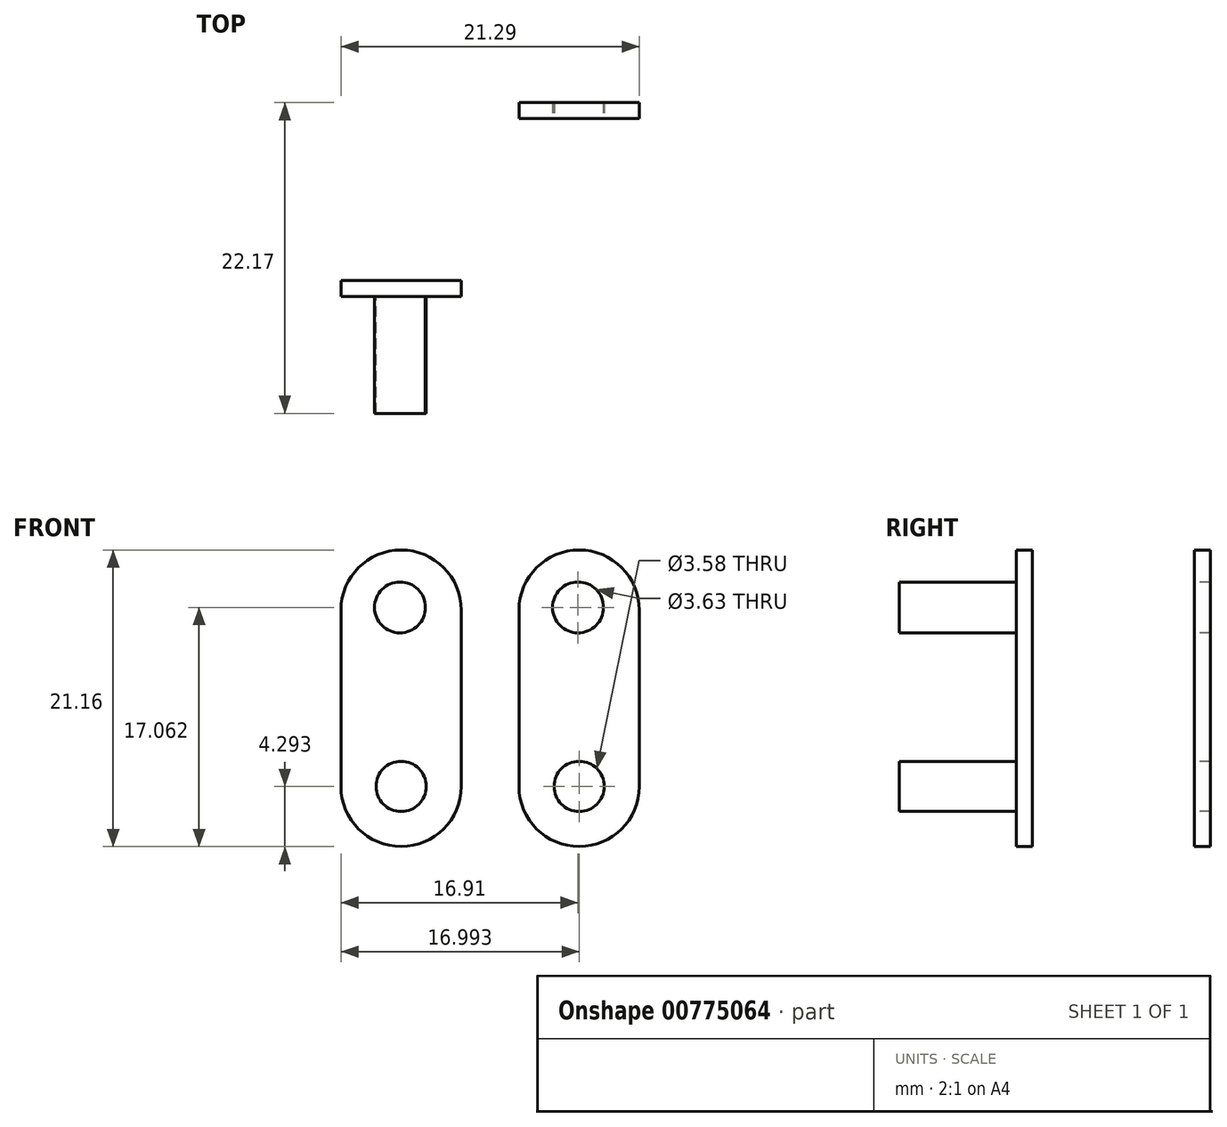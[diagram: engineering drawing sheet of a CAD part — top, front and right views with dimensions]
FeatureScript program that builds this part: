
annotation { "Feature Type Name" : "Feature", "Feature Type Description" : "" }
export const myFeature = defineFeature(function(context is Context, id is Id, definition is map)
    precondition{}
    {
        {
            var Q0;
            Q0=qCreatedBy(makeId("Front.planeOp"),FACE);
            var sketch = newSketch(context, id + "F0", { "sketchPlane" : qUnion([Q0])});
            skLineSegment(sketch, "E0.left", {"start": v(0, 4.3) * mm, "end": v(0, 16.87) * mm});
            skLineSegment(sketch, "E0.right", {"start": v(8.59, 4.3) * mm, "end": v(8.59, 16.87) * mm});
            skArc(sketch, "E1", {"start": v(8.59, 16.87) * mm, "mid": v(4.3, 21.16) * mm, "end": v(0, 16.87) * mm});
            skArc(sketch, "E2", {"start": v(0, 4.3) * mm, "mid": v(4.3, 0) * mm, "end": v(8.59, 4.3) * mm});
            skSolve(sketch);
        }
        {
            var Q0;
            Q0 = qSketchRegion(id + "F0", true);
            extrude(context, id + "F1", {"entities" : qUnion([Q0]), "depth" : 1.14 * mm, "offsetDistance" : 25.4 * mm});
        }
        {
            var Q0;
            Q0=makeQuery(id+"F1.opExtrude","CAP_FACE",FACE,{"disambiguationData":[OSD([sQuery(id+"F0.wireOp",EDGE,"E0.left"),sQuery(id+"F0.wireOp",EDGE,"E0.right"),sQuery(id+"F0.wireOp",EDGE,"E1"),sQuery(id+"F0.wireOp",EDGE,"E2")])],"isStart":false});
            var sketch = newSketch(context, id + "F2", { "sketchPlane" : qUnion([Q0])});
            skCircle(sketch, "E3", {"center": v(4.3, 4.3) * mm, "radius": 1.8 * mm});
            skCircle(sketch, "E4", {"center": v(4.2, 17.06) * mm, "radius": 1.82 * mm});
            skSolve(sketch);
        }
        {
            var Q0;
            Q0 = qSketchRegion(id + "F2", true);
            extrude(context, id + "F3", {"entities" : qUnion([Q0]), "operationType" : NewBodyOperationType.ADD, "depth" : 8.33 * mm, "offsetDistance" : 25.4 * mm});
        }
        {
            var Q0;
            Q0=makeQuery(id+"F1.opExtrude","SWEPT_BODY",BODY,{"disambiguationData":[OSD([sQuery(id+"F0.wireOp",EDGE,"E0.left"),sQuery(id+"F0.wireOp",EDGE,"E0.right"),sQuery(id+"F0.wireOp",EDGE,"E1"),sQuery(id+"F0.wireOp",EDGE,"E2")])]});
            transform(context, id + "F4", {"entities" : qUnion([Q0]), "transformType" : TransformType.TRANSLATION_3D, "dx" : 12.7 * mm, "dy" : 12.7 * mm, "dz" : 0 * mm, "makeCopy" : true});
        }
        {
            var Q0;
            Q0=makeQuery(id+"F4.opPattern","COPY",FACE,{"derivedFrom":makeQuery(id+"F3.opExtrude","CAP_FACE",FACE,{"disambiguationData":[OSD([sQuery(id+"F2.wireOp",EDGE,"E4")])],"isStart":false}),"instanceName":"1"});
            var Q1;
            Q1=makeQuery(id+"F4.opPattern","COPY",FACE,{"derivedFrom":makeQuery(id+"F3.opExtrude","CAP_FACE",FACE,{"disambiguationData":[OSD([sQuery(id+"F2.wireOp",EDGE,"E3")])],"isStart":false}),"instanceName":"1"});
            extrude(context, id + "F5", {"entities" : qUnion([Q0, Q1]), "operationType" : NewBodyOperationType.REMOVE, "oppositeDirection" : true, "depth" : 25.4 * mm, "offsetDistance" : 25.4 * mm});
        }
    });
